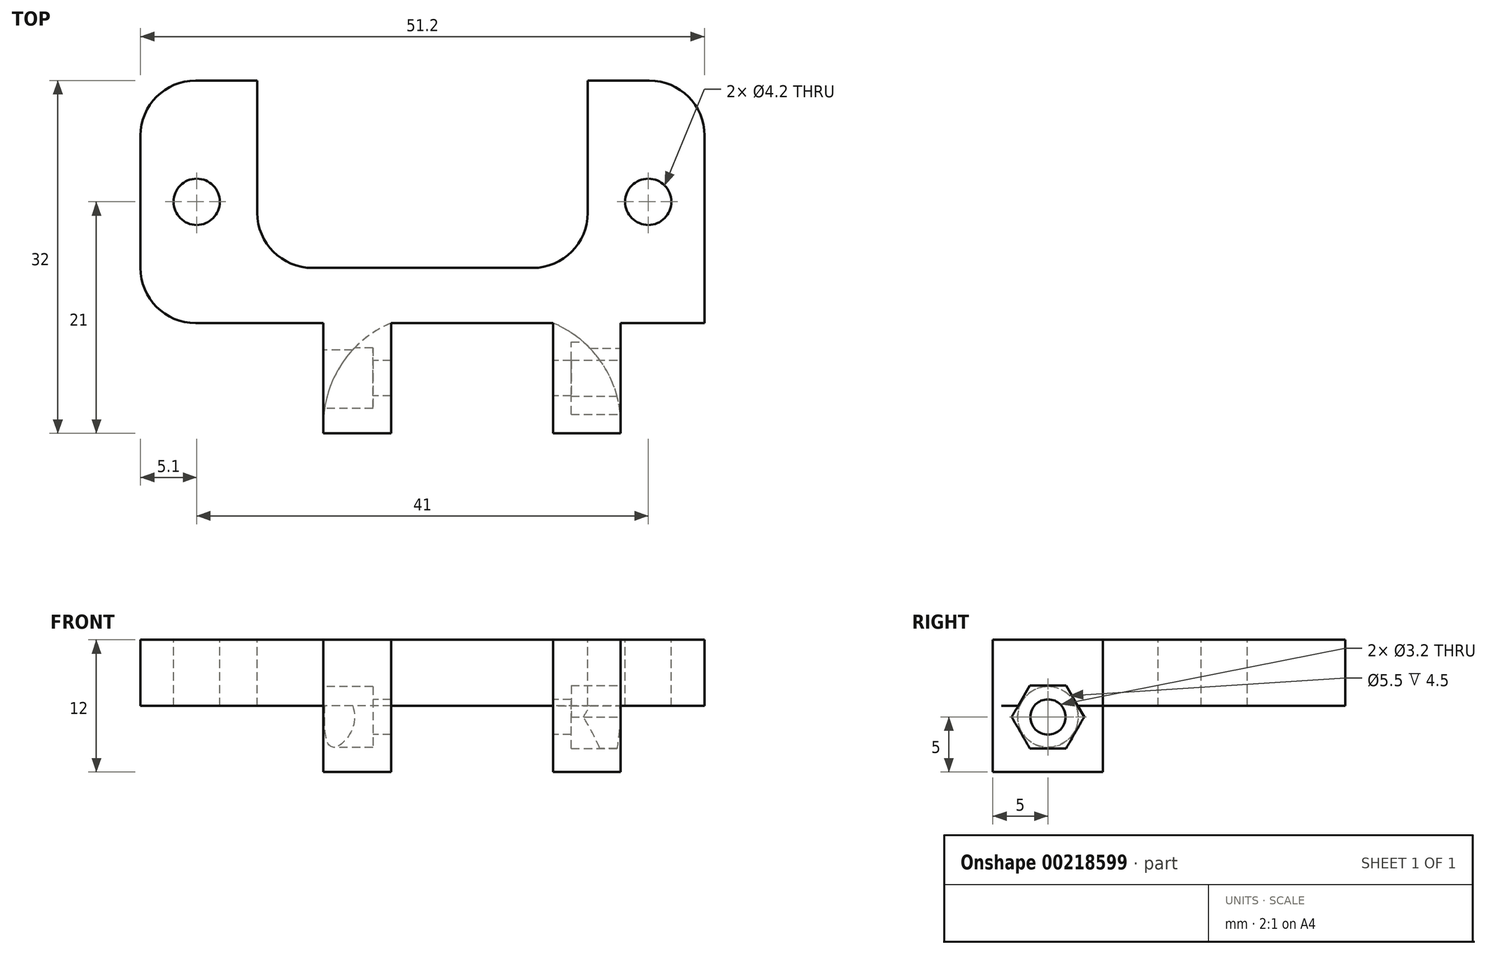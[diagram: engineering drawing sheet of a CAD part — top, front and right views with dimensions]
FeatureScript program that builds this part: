
annotation { "Feature Type Name" : "Feature", "Feature Type Description" : "" }
export const myFeature = defineFeature(function(context is Context, id is Id, definition is map)
    precondition{}
    {
        {
            var Q0;
            Q0=qCreatedBy(makeId("Top.planeOp"),FACE);
            var sketch = newSketch(context, id + "F0", { "sketchPlane" : qUnion([Q0])});
            skLineSegment(sketch, "E0.bottom", {"start": v(25.6, 11) * mm, "end": v(-25.6, 11) * mm});
            skLineSegment(sketch, "E0.top", {"start": v(25.6, -11) * mm, "end": v(-25.6, -11) * mm});
            skLineSegment(sketch, "E0.left", {"start": v(25.6, 11) * mm, "end": v(25.6, -11) * mm});
            skLineSegment(sketch, "E0.right", {"start": v(-25.6, 11) * mm, "end": v(-25.6, -11) * mm});
            skPoint(sketch, "E0.middle", {"position": v(0, 0) * mm});
            skSolve(sketch);
        }
        {
            var Q0;
            Q0=makeQuery(id+"F0.imprint","IMPRINT",FACE,{"disambiguationData":[TD([[makeQuery(id+"F0.imprint","IMPRINT",EDGE,{"derivedFrom":sQuery(id+"F0.wireOp",EDGE,"E0.bottom")}),1.0]])]});
            extrude(context, id + "F1", {"entities" : qUnion([Q0]), "depth" : 6 * mm, "offsetDistance" : 25 * mm});
        }
        {
            var Q0;
            Q0=makeQuery(id+"F1.opExtrude","CAP_FACE",FACE,{"disambiguationData":[OSD([sQuery(id+"F0.wireOp",EDGE,"E0.bottom"),sQuery(id+"F0.wireOp",EDGE,"E0.top"),sQuery(id+"F0.wireOp",EDGE,"E0.left"),sQuery(id+"F0.wireOp",EDGE,"E0.right")])],"isStart":false});
            var sketch = newSketch(context, id + "F2", { "sketchPlane" : qUnion([Q0])});
            skCircle(sketch, "E1", {"center": v(-20.5, 0) * mm, "radius": 2.1 * mm});
            skCircle(sketch, "E2", {"center": v(20.5, 0) * mm, "radius": 2.1 * mm});
            skLineSegment(sketch, "E3", {"start": v(0, 0) * mm, "end": v(0, -8.07) * mm, "construction": true});
            skSolve(sketch);
        }
        {
            var Q0;
            Q0 = qSketchRegion(id + "F2", true);
            extrude(context, id + "F3", {"entities" : qUnion([Q0]), "operationType" : NewBodyOperationType.REMOVE, "endBound" : BoundingType.THROUGH_ALL, "oppositeDirection" : true, "depth" : 25 * mm, "offsetDistance" : 25 * mm});
        }
        {
            var Q0;
            Q0=makeQuery(id+"F1.opExtrude","CAP_FACE",FACE,{"disambiguationData":[OSD([sQuery(id+"F0.wireOp",EDGE,"E0.bottom"),sQuery(id+"F0.wireOp",EDGE,"E0.top"),sQuery(id+"F0.wireOp",EDGE,"E0.left"),sQuery(id+"F0.wireOp",EDGE,"E0.right")])],"isStart":false});
            var sketch = newSketch(context, id + "F4", { "sketchPlane" : qUnion([Q0])});
            skPoint(sketch, "E4", {"position": v(20.5, 0) * mm});
            skArc(sketch, "E5", {"start": v(-1.5, 0) * mm, "mid": v(4.5, -6) * mm, "end": v(10.5, 0) * mm});
            skLineSegment(sketch, "E6", {"start": v(10.5, 0) * mm, "end": v(10.5, 11) * mm});
            skLineSegment(sketch, "E7", {"start": v(10.5, 11) * mm, "end": v(-1.5, 11) * mm});
            skLineSegment(sketch, "E8", {"start": v(-1.5, 11) * mm, "end": v(-1.5, 0) * mm});
            skSolve(sketch);
        }
        {
            var Q0;
            Q0 = qSketchRegion(id + "F4", true);
            extrude(context, id + "F5", {"entities" : qUnion([Q0]), "operationType" : NewBodyOperationType.REMOVE, "endBound" : BoundingType.THROUGH_ALL, "oppositeDirection" : true, "depth" : 25 * mm, "offsetDistance" : 25 * mm});
        }
        {
            var Q0;
            Q0=makeQuery(id+"F5.boolean.opBoolean","COPY",FACE,{"derivedFrom":makeQuery(id+"F5.opExtrude","SWEPT_FACE",FACE,{"disambiguationData":[OSD([sQuery(id+"F4.wireOp",EDGE,"E6")])]})});
            var Q1;
            Q1=makeQuery(id+"F5.boolean.opBoolean","COPY",FACE,{"derivedFrom":makeQuery(id+"F5.opExtrude","SWEPT_FACE",FACE,{"disambiguationData":[OSD([sQuery(id+"F4.wireOp",EDGE,"E8")])]})});
            cPlane(context, id + "F6", {"entities" : qUnion([Q0, Q1]), "cplaneType" : CPlaneType.MID_PLANE, "offset" : 25 * mm, "width" : 150 * mm, "height" : 150 * mm});
        }
        {
            var Q0;
            Q0=qCreatedBy(id+"F6.planeOp",FACE);
            var sketch = newSketch(context, id + "F7", { "sketchPlane" : qUnion([Q0])});
            skLineSegment(sketch, "E9", {"start": v(11, 6) * mm, "end": v(21, 6) * mm});
            skLineSegment(sketch, "E10", {"start": v(11, 0) * mm, "end": v(11, 6) * mm});
            skLineSegment(sketch, "E11", {"start": v(21, 6) * mm, "end": v(21, -6) * mm});
            skLineSegment(sketch, "E12", {"start": v(21, -6) * mm, "end": v(11, -6) * mm});
            skLineSegment(sketch, "E13", {"start": v(11, -6) * mm, "end": v(11, 0) * mm});
            skSolve(sketch);
        }
        {
            var Q0;
            Q0 = qSketchRegion(id + "F7", true);
            extrude(context, id + "F8", {"entities" : qUnion([Q0]), "operationType" : NewBodyOperationType.ADD, "depth" : 27 * mm, "offsetDistance" : 25 * mm, "symmetric" : true});
        }
        {
            var Q0;
            Q0=makeQuery(id+"F8.opExtrude","SWEPT_FACE",FACE,{"disambiguationData":[OSD([sQuery(id+"F7.wireOp",EDGE,"E12")])]});
            var sketch = newSketch(context, id + "F9", { "sketchPlane" : qUnion([Q0])});
            skLineSegment(sketch, "E14.bottom", {"start": v(-2.85, 11) * mm, "end": v(11.85, 11) * mm});
            skLineSegment(sketch, "E14.top", {"start": v(-2.85, 21) * mm, "end": v(11.85, 21) * mm});
            skLineSegment(sketch, "E14.left", {"start": v(-2.85, 11) * mm, "end": v(-2.85, 21) * mm});
            skLineSegment(sketch, "E14.right", {"start": v(11.85, 11) * mm, "end": v(11.85, 21) * mm});
            skPoint(sketch, "E15", {"position": v(4.5, 21) * mm});
            skSolve(sketch);
        }
        {
            var Q0;
            Q0 = qSketchRegion(id + "F9", true);
            extrude(context, id + "F10", {"entities" : qUnion([Q0]), "operationType" : NewBodyOperationType.REMOVE, "endBound" : BoundingType.THROUGH_ALL, "oppositeDirection" : true, "depth" : 25 * mm, "offsetDistance" : 25 * mm});
        }
        {
            var Q0;
            {var subQ0=sQuery(id+"F7.wireOp",EDGE,"E13");var subQ1=sQuery(id+"F7.wireOp",EDGE,"E10");Q0=makeQuery(id+"F8.boolean.opBoolean","SPLIT",EDGE,{"disambiguationData":[topologyDisambiguationEdgeConnected([makeQuery(id+"F1.opExtrude","SWEPT_FACE",FACE,{"disambiguationData":[OSD([sQuery(id+"F0.wireOp",EDGE,"E0.top")])]})])],"derivedFrom":makeQuery(id+"F8.opExtrude","CAP_EDGE",EDGE,{"disambiguationData":[OSD([subQ1,subQ0])],"isStart":false})});}
            var Q1;
            {var subQ0=sQuery(id+"F7.wireOp",EDGE,"E13");var subQ1=sQuery(id+"F7.wireOp",EDGE,"E10");Q1=makeQuery(id+"F8.boolean.opBoolean","SPLIT",EDGE,{"disambiguationData":[topologyDisambiguationEdgeConnected([makeQuery(id+"F1.opExtrude","SWEPT_FACE",FACE,{"disambiguationData":[OSD([sQuery(id+"F0.wireOp",EDGE,"E0.top")])]})])],"derivedFrom":makeQuery(id+"F8.opExtrude","CAP_EDGE",EDGE,{"disambiguationData":[OSD([subQ1,subQ0])],"isStart":true})});}
            fillet(context, id + "F11", {"entities" : qUnion([Q0, Q1]), "radius" : 10 * mm, "tangentPropagation" : true, "allowEdgeOverflow" : false});
        }
        {
            var Q0;
            Q0=makeQuery(id+"F8.opExtrude","CAP_FACE",FACE,{"disambiguationData":[OSD([sQuery(id+"F7.wireOp",EDGE,"E9"),sQuery(id+"F7.wireOp",EDGE,"E10"),sQuery(id+"F7.wireOp",EDGE,"E11"),sQuery(id+"F7.wireOp",EDGE,"E12"),sQuery(id+"F7.wireOp",EDGE,"E13")])],"isStart":false});
            var sketch = newSketch(context, id + "F12", { "sketchPlane" : qUnion([Q0])});
            skCircle(sketch, "E16", {"center": v(16, -1) * mm, "radius": 1.6 * mm});
            skSolve(sketch);
        }
        {
            var Q0;
            Q0 = qSketchRegion(id + "F12", true);
            extrude(context, id + "F13", {"entities" : qUnion([Q0]), "operationType" : NewBodyOperationType.REMOVE, "endBound" : BoundingType.THROUGH_ALL, "oppositeDirection" : true, "depth" : 25 * mm, "offsetDistance" : 25 * mm, "hasSecondDirection" : true, "secondDirectionBound" : BoundingType.THROUGH_ALL, "secondDirectionOppositeDirection" : false, "secondDirectionDepth" : 25 * mm});
        }
        {
            var Q0;
            Q0=makeQuery(id+"F8.opExtrude","CAP_FACE",FACE,{"disambiguationData":[OSD([sQuery(id+"F7.wireOp",EDGE,"E9"),sQuery(id+"F7.wireOp",EDGE,"E10"),sQuery(id+"F7.wireOp",EDGE,"E11"),sQuery(id+"F7.wireOp",EDGE,"E12"),sQuery(id+"F7.wireOp",EDGE,"E13")])],"isStart":false});
            var sketch = newSketch(context, id + "F14", { "sketchPlane" : qUnion([Q0])});
            skCircle(sketch, "E17", {"center": v(16, -1) * mm, "radius": 2.75 * mm});
            skSolve(sketch);
        }
        {
            var Q0;
            Q0 = qSketchRegion(id + "F14", true);
            extrude(context, id + "F15", {"entities" : qUnion([Q0]), "operationType" : NewBodyOperationType.REMOVE, "oppositeDirection" : true, "depth" : 4.5 * mm, "offsetDistance" : 25 * mm, "hasSecondDirection" : true, "secondDirectionBound" : BoundingType.THROUGH_ALL, "secondDirectionOppositeDirection" : false, "secondDirectionDepth" : 25 * mm});
        }
        {
            var Q0;
            Q0=makeQuery(id+"F8.opExtrude","CAP_FACE",FACE,{"disambiguationData":[OSD([sQuery(id+"F7.wireOp",EDGE,"E9"),sQuery(id+"F7.wireOp",EDGE,"E10"),sQuery(id+"F7.wireOp",EDGE,"E11"),sQuery(id+"F7.wireOp",EDGE,"E12"),sQuery(id+"F7.wireOp",EDGE,"E13")])],"isStart":true});
            var sketch = newSketch(context, id + "F16", { "sketchPlane" : qUnion([Q0])});
            skCircle(sketch, "E18.cCircle", {"center": v(-16, -1) * mm, "radius": 2.85 * mm, "construction": true});
            skLineSegment(sketch, "E18.0", {"start": v(-12.7, -1) * mm, "end": v(-14.35, -3.85) * mm});
            skLineSegment(sketch, "E18.1", {"start": v(-14.35, -3.85) * mm, "end": v(-17.65, -3.85) * mm});
            skLineSegment(sketch, "E18.2", {"start": v(-17.65, -3.85) * mm, "end": v(-19.3, -1) * mm});
            skLineSegment(sketch, "E18.3", {"start": v(-19.3, -1) * mm, "end": v(-17.65, 1.85) * mm});
            skLineSegment(sketch, "E18.4", {"start": v(-17.65, 1.85) * mm, "end": v(-14.35, 1.85) * mm});
            skLineSegment(sketch, "E18.5", {"start": v(-14.35, 1.85) * mm, "end": v(-12.7, -1) * mm});
            skPoint(sketch, "E18.0.midPoint", {"position": v(-13.53, -2.43) * mm});
            skSolve(sketch);
        }
        {
            var Q0;
            Q0 = qSketchRegion(id + "F16", true);
            extrude(context, id + "F17", {"entities" : qUnion([Q0]), "operationType" : NewBodyOperationType.REMOVE, "oppositeDirection" : true, "depth" : 4.5 * mm, "offsetDistance" : 25 * mm, "hasSecondDirection" : true, "secondDirectionOppositeDirection" : false, "secondDirectionDepth" : 25 * mm});
        }
        {
            var Q0;
            Q0=makeQuery(id+"F8.boolean.opBoolean","MERGE",FACE,{"derivedFrom":[makeQuery(id+"F1.opExtrude","CAP_FACE",FACE,{"disambiguationData":[OSD([sQuery(id+"F0.wireOp",EDGE,"E0.bottom"),sQuery(id+"F0.wireOp",EDGE,"E0.top"),sQuery(id+"F0.wireOp",EDGE,"E0.left"),sQuery(id+"F0.wireOp",EDGE,"E0.right")])],"isStart":false}),makeQuery(id+"F8.opExtrude","SWEPT_FACE",FACE,{"disambiguationData":[OSD([sQuery(id+"F7.wireOp",EDGE,"E9")])]})]});
            var sketch = newSketch(context, id + "F18", { "sketchPlane" : qUnion([Q0])});
            skPoint(sketch, "E19.oppositeSnap0", {"position": v(4.5, -6) * mm});
            skLineSegment(sketch, "E19.bottom", {"start": v(-15, 11) * mm, "end": v(15, 11) * mm});
            skLineSegment(sketch, "E19.top", {"start": v(-15, -6) * mm, "end": v(15, -6) * mm});
            skLineSegment(sketch, "E19.left", {"start": v(-15, 11) * mm, "end": v(-15, -6) * mm});
            skLineSegment(sketch, "E19.right", {"start": v(15, 11) * mm, "end": v(15, -6) * mm});
            skPoint(sketch, "E20", {"position": v(0, 11) * mm});
            skLineSegment(sketch, "E21", {"start": v(20.5, 0) * mm, "end": v(-20.5, 0) * mm, "construction": true});
            skSolve(sketch);
        }
        {
            var Q0;
            Q0 = qSketchRegion(id + "F18", true);
            extrude(context, id + "F19", {"entities" : qUnion([Q0]), "operationType" : NewBodyOperationType.REMOVE, "endBound" : BoundingType.THROUGH_ALL, "oppositeDirection" : true, "depth" : 25 * mm, "offsetDistance" : 25 * mm});
        }
        {
            var Q0;
            Q0=makeQuery(id+"F19.boolean.opBoolean","COPY",EDGE,{"derivedFrom":makeQuery(id+"F19.opExtrude","SWEPT_EDGE",EDGE,{"disambiguationData":[OSD([sQuery(id+"F18.wireOp",EDGE,"E19.top"),sQuery(id+"F18.wireOp",EDGE,"E19.left")])]})});
            var Q1;
            Q1=makeQuery(id+"F19.boolean.opBoolean","COPY",EDGE,{"derivedFrom":makeQuery(id+"F19.opExtrude","SWEPT_EDGE",EDGE,{"disambiguationData":[OSD([sQuery(id+"F18.wireOp",EDGE,"E19.top"),sQuery(id+"F18.wireOp",EDGE,"E19.right")])]})});
            var Q2;
            Q2=makeQuery(id+"F1.opExtrude","SWEPT_EDGE",EDGE,{"disambiguationData":[OSD([sQuery(id+"F0.wireOp",EDGE,"E0.top"),sQuery(id+"F0.wireOp",EDGE,"E0.right")])]});
            var Q3;
            {var subQ0=sQuery(id+"F7.wireOp",EDGE,"E13");var subQ1=sQuery(id+"F7.wireOp",EDGE,"E10");Q3=makeQuery(id+"F11.opFillet","BLEND_EDGE",EDGE,{"blendedFrom":[makeQuery(id+"F8.boolean.opBoolean","SPLIT",EDGE,{"disambiguationData":[topologyDisambiguationEdgeConnected([makeQuery(id+"F1.opExtrude","SWEPT_FACE",FACE,{"disambiguationData":[OSD([sQuery(id+"F0.wireOp",EDGE,"E0.top")])]})])],"derivedFrom":makeQuery(id+"F8.opExtrude","CAP_EDGE",EDGE,{"disambiguationData":[OSD([subQ1,subQ0])],"isStart":true})}),makeQuery(id+"F1.opExtrude","SWEPT_FACE",FACE,{"disambiguationData":[OSD([sQuery(id+"F0.wireOp",EDGE,"E0.left")])]})],"blendedInto":[makeQuery(id+"F1.opExtrude","SWEPT_FACE",FACE,{"disambiguationData":[OSD([sQuery(id+"F0.wireOp",EDGE,"E0.left")])]})]});}
            var Q4;
            Q4=makeQuery(id+"F1.opExtrude","SWEPT_EDGE",EDGE,{"disambiguationData":[OSD([sQuery(id+"F0.wireOp",EDGE,"E0.bottom"),sQuery(id+"F0.wireOp",EDGE,"E0.left")])]});
            var Q5;
            Q5=makeQuery(id+"F19.boolean.opBoolean","COPY",EDGE,{"derivedFrom":makeQuery(id+"F19.opExtrude","SWEPT_EDGE",EDGE,{"disambiguationData":[OSD([sQuery(id+"F0.wireOp",EDGE,"E0.bottom"),sQuery(id+"F18.wireOp",EDGE,"E19.bottom"),sQuery(id+"F18.wireOp",EDGE,"E19.right")])]})});
            var Q6;
            Q6=makeQuery(id+"F1.opExtrude","SWEPT_EDGE",EDGE,{"disambiguationData":[OSD([sQuery(id+"F0.wireOp",EDGE,"E0.bottom"),sQuery(id+"F0.wireOp",EDGE,"E0.right")])]});
            var Q7;
            Q7=makeQuery(id+"F19.boolean.opBoolean","COPY",EDGE,{"derivedFrom":makeQuery(id+"F19.opExtrude","SWEPT_EDGE",EDGE,{"disambiguationData":[OSD([sQuery(id+"F0.wireOp",EDGE,"E0.bottom"),sQuery(id+"F18.wireOp",EDGE,"E19.bottom"),sQuery(id+"F18.wireOp",EDGE,"E19.left")])]})});
            fillet(context, id + "F20", {"entities" : qUnion([Q0, Q1, Q2, Q3, Q4, Q5, Q6, Q7]), "radius" : 5 * mm, "tangentPropagation" : true, "allowEdgeOverflow" : false});
        }
    });
